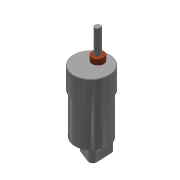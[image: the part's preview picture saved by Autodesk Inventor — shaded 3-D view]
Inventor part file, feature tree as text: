
AUTODESK INVENTOR PART (.ipt)
format: ipt  version: 2013 (Build 170138000, 138)  size: 252,416 bytes
history: native  units: in
note: dims shown in document units (in); Inventor stores cm internally (conversion verified against a paired STEP export)
features: extrude x4, sketch x4, fillet x2, other x1, imported_body x1
ambient origin geometry x8: Origin, YZ Plane, XZ Plane, XY Plane, X Axis, Y Axis, Z Axis, Center Point
bodies: Solid2 (feature_tree)
feature tree (12):
  other  "DC_MOTOR_2011"
  imported_body  "Base1"
  extrude  "Extrusion1"  Depth=0.5909in
  extrude  "Extrusion2"  Depth=0.4528in
  extrude  "Extrusion3"  Depth=0.1654in TaperAngle=0.0deg
  fillet  "Fillet1"  Radius=0.748in
  fillet  "Fillet2"  Radius=0.4331in
  extrude  "Extrusion4"  Depth=0.2165in
  sketch  "Sketch1"  dims[d0=0.315in d1=0.5909in]
  sketch  "Sketch2"  dims[d3=0.3436in d5=0.4528in]
  sketch  "Sketch3"  dims[d6=0.4528in d7=0.1654in d8=0.0in d9=0.748in d11=0.4331in]
  sketch  "Sketch4"  dims[d12=0.3661in d13=0.0in d14=0.2165in d16=0.0472in d17=0.0in d18=0.0197in d19=0.0787in d20=0.1181in d21=0.1181in d22=0.5906in d23=0.0in]
